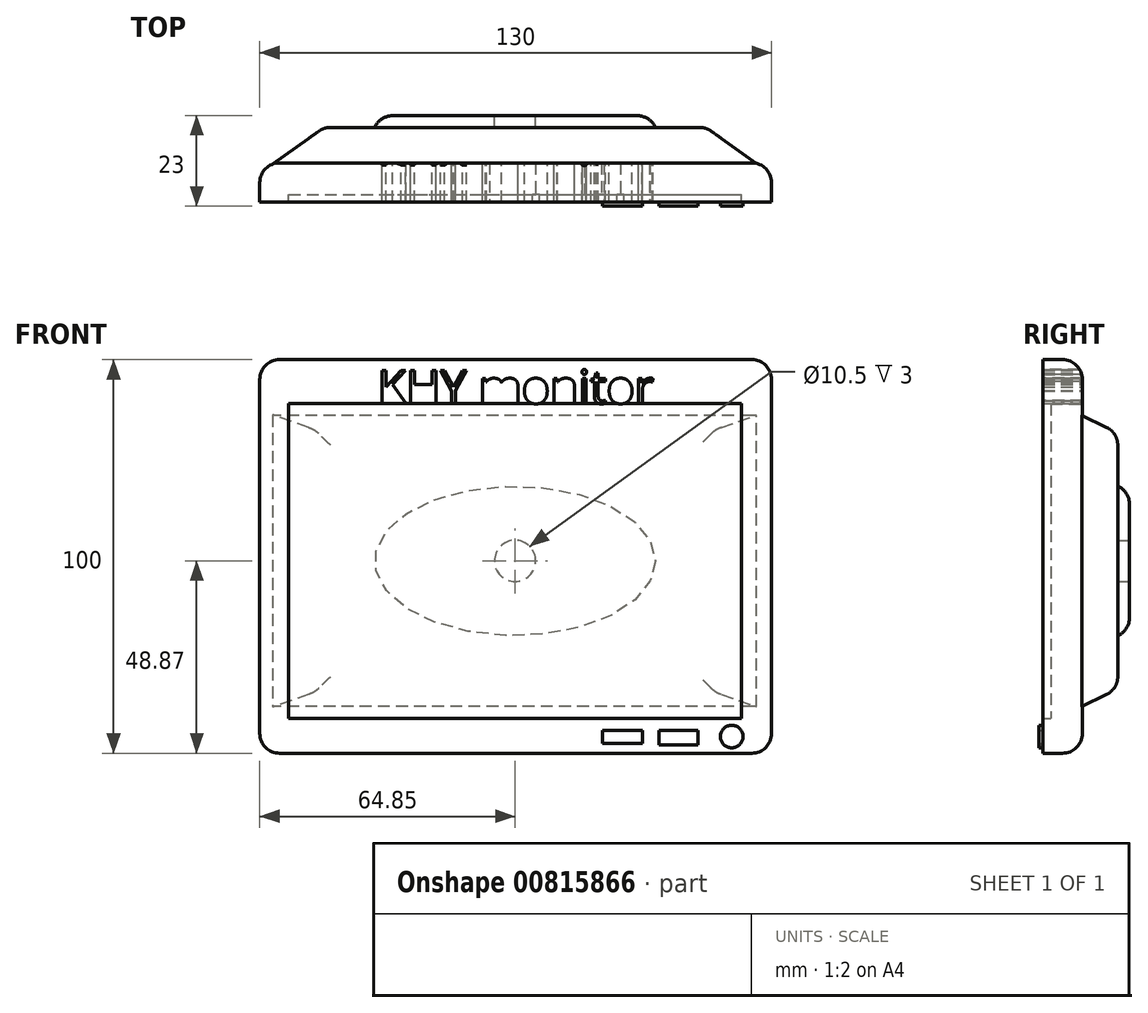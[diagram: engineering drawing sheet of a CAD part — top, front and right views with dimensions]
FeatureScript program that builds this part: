
annotation { "Feature Type Name" : "Feature", "Feature Type Description" : "" }
export const myFeature = defineFeature(function(context is Context, id is Id, definition is map)
    precondition{}
    {
        {
            var Q0;
            Q0=qCreatedBy(makeId("Front.planeOp"),FACE);
            var sketch = newSketch(context, id + "F0", { "sketchPlane" : qUnion([Q0])});
            skLineSegment(sketch, "E0.bottom", {"start": v(-59.85, 51.13) * mm, "end": v(60.15, 51.13) * mm});
            skLineSegment(sketch, "E0.top", {"start": v(-59.85, -48.87) * mm, "end": v(60.15, -48.87) * mm});
            skLineSegment(sketch, "E0.left", {"start": v(-64.85, 46.13) * mm, "end": v(-64.85, -43.87) * mm});
            skLineSegment(sketch, "E0.right", {"start": v(65.15, 46.13) * mm, "end": v(65.15, -43.87) * mm});
            skPoint(sketch, "E1.visualSharp", {"position": v(-64.85, 51.13) * mm});
            skArc(sketch, "E1.filletArc", {"start": v(-59.85, 51.13) * mm, "mid": v(-63.38, 49.67) * mm, "end": v(-64.85, 46.13) * mm});
            skPoint(sketch, "E2.visualSharp", {"position": v(65.15, 51.13) * mm});
            skArc(sketch, "E2.filletArc", {"start": v(65.15, 46.13) * mm, "mid": v(63.69, 49.67) * mm, "end": v(60.15, 51.13) * mm});
            skPoint(sketch, "E3.visualSharp", {"position": v(65.15, -48.87) * mm});
            skArc(sketch, "E3.filletArc", {"start": v(60.15, -48.87) * mm, "mid": v(63.69, -47.4) * mm, "end": v(65.15, -43.87) * mm});
            skPoint(sketch, "E4.visualSharp", {"position": v(-64.85, -48.87) * mm});
            skArc(sketch, "E4.filletArc", {"start": v(-64.85, -43.87) * mm, "mid": v(-63.38, -47.4) * mm, "end": v(-59.85, -48.87) * mm});
            skLineSegment(sketch, "E5.bottom", {"start": v(-57.5, 40) * mm, "end": v(57.5, 40) * mm});
            skLineSegment(sketch, "E5.top", {"start": v(-57.5, -40) * mm, "end": v(57.5, -40) * mm});
            skLineSegment(sketch, "E5.left", {"start": v(-57.5, 40) * mm, "end": v(-57.5, -40) * mm});
            skLineSegment(sketch, "E5.right", {"start": v(57.5, 40) * mm, "end": v(57.5, -40) * mm});
            skPoint(sketch, "E5.middle", {"position": v(0, 0) * mm});
            skText(sketch, "E6", { "text": "KHY monitor", "fontName": "OpenSans-Regular.ttf"});
            const initialGuessF0  = {"E6": [-0.0349, 0.04, 1, 0, 0.0085]};
            skSetInitialGuess(sketch, initialGuessF0);
            skSolve(sketch);
        }
        {
            var Q0;
            Q0=makeQuery(id+"F0.imprint","IMPRINT",FACE,{"disambiguationData":[TD([[makeQuery(id+"F0.imprint","IMPRINT",EDGE,{"derivedFrom":sQuery(id+"F0.wireOp",EDGE,"E0.bottom")}),-1.0]])]});
            extrude(context, id + "F1", {"entities" : qUnion([Q0]), "depth" : 10 * mm, "offsetDistance" : 25 * mm});
        }
        {
            var Q0;
            Q0=makeQuery(id+"F0.imprint","IMPRINT",FACE,{"disambiguationData":[TD([[makeQuery(id+"F0.imprint","IMPRINT",EDGE,{"derivedFrom":sQuery(id+"F0.wireOp",EDGE,"E5.top")}),1.0]])]});
            extrude(context, id + "F2", {"entities" : qUnion([Q0]), "operationType" : NewBodyOperationType.ADD, "depth" : 8 * mm, "offsetDistance" : 25 * mm});
        }
        {
            var Q0;
            Q0=qCreatedBy(makeId("Front.planeOp"),FACE);
            cPlane(context, id + "F3", {"entities" : qUnion([Q0]), "cplaneType" : CPlaneType.OFFSET, "offset" : 9 * mm, "oppositeDirection" : true, "width" : 150 * mm, "height" : 150 * mm});
        }
        {
            var Q0;
            Q0=qCreatedBy(id+"F3.planeOp",FACE);
            var sketch = newSketch(context, id + "F4", { "sketchPlane" : qUnion([Q0])});
            skLineSegment(sketch, "E7.bottom", {"start": v(48.52, 32.56) * mm, "end": v(-48.52, 32.56) * mm});
            skLineSegment(sketch, "E7.top", {"start": v(48.52, -32.56) * mm, "end": v(-48.52, -32.56) * mm});
            skLineSegment(sketch, "E7.left", {"start": v(48.52, 32.56) * mm, "end": v(48.52, -32.56) * mm});
            skLineSegment(sketch, "E7.right", {"start": v(-48.52, 32.56) * mm, "end": v(-48.52, -32.56) * mm});
            skPoint(sketch, "E7.middle", {"position": v(0, 0) * mm});
            skSolve(sketch);
        }
        {
            var Q0;
            Q0=qCreatedBy(makeId("Front.planeOp"),FACE);
            var sketch = newSketch(context, id + "F5", { "sketchPlane" : qUnion([Q0])});
            skLineSegment(sketch, "E8.bottom", {"start": v(61.13, 36.93) * mm, "end": v(-61.13, 36.93) * mm});
            skLineSegment(sketch, "E8.top", {"start": v(61.13, -36.93) * mm, "end": v(-61.13, -36.93) * mm});
            skLineSegment(sketch, "E8.left", {"start": v(61.13, 36.93) * mm, "end": v(61.13, -36.93) * mm});
            skLineSegment(sketch, "E8.right", {"start": v(-61.13, 36.93) * mm, "end": v(-61.13, -36.93) * mm});
            skPoint(sketch, "E8.middle", {"position": v(0, 0) * mm});
            skSolve(sketch);
        }
        {
            var Q1;
            Q1=makeQuery(id+"F4.imprint","IMPRINT",FACE,{"disambiguationData":[TD([[makeQuery(id+"F4.imprint","IMPRINT",EDGE,{"derivedFrom":sQuery(id+"F4.wireOp",EDGE,"E7.bottom")}),1.0]])]});
            var Q2;
            Q2=makeQuery(id+"F5.imprint","IMPRINT",FACE,{"disambiguationData":[TD([[makeQuery(id+"F5.imprint","IMPRINT",EDGE,{"derivedFrom":sQuery(id+"F5.wireOp",EDGE,"E8.bottom")}),1.0]])]});
            loft(context, id + "F6", {"operationType" : NewBodyOperationType.ADD, "sheetProfilesArray" : [{ "sheetProfileEntities" : qUnion([Q1]) }, { "sheetProfileEntities" : qUnion([Q2]) }]});
        }
        {
            var Q0;
            Q0=makeQuery(id+"F1.opExtrude","CAP_FACE",FACE,{"disambiguationData":[OSD([sQuery(id+"F0.wireOp",EDGE,"E0.bottom"),sQuery(id+"F0.wireOp",EDGE,"E0.top"),sQuery(id+"F0.wireOp",EDGE,"E0.left"),sQuery(id+"F0.wireOp",EDGE,"E0.right"),sQuery(id+"F0.wireOp",EDGE,"E1.filletArc"),sQuery(id+"F0.wireOp",EDGE,"E2.filletArc"),sQuery(id+"F0.wireOp",EDGE,"E3.filletArc"),sQuery(id+"F0.wireOp",EDGE,"E4.filletArc"),sQuery(id+"F0.wireOp",EDGE,"E5.bottom"),sQuery(id+"F0.wireOp",EDGE,"E5.top"),sQuery(id+"F0.wireOp",EDGE,"E5.left"),sQuery(id+"F0.wireOp",EDGE,"E5.right"),sQuery(id+"F0.wireOp",EDGE,"E6.sketch_text.stroke-5"),sQuery(id+"F0.wireOp",EDGE,"E6.sketch_text.stroke-6"),sQuery(id+"F0.wireOp",EDGE,"E6.sketch_text.stroke-7"),sQuery(id+"F0.wireOp",EDGE,"E6.sketch_text.stroke-8"),sQuery(id+"F0.wireOp",EDGE,"E6.sketch_text.stroke-9"),sQuery(id+"F0.wireOp",EDGE,"E6.sketch_text.stroke-10"),sQuery(id+"F0.wireOp",EDGE,"E6.sketch_text.stroke-11"),sQuery(id+"F0.wireOp",EDGE,"E6.sketch_text.stroke-17"),sQuery(id+"F0.wireOp",EDGE,"E6.sketch_text.stroke-18"),sQuery(id+"F0.wireOp",EDGE,"E6.sketch_text.stroke-19"),sQuery(id+"F0.wireOp",EDGE,"E6.sketch_text.stroke-20"),sQuery(id+"F0.wireOp",EDGE,"E6.sketch_text.stroke-21"),sQuery(id+"F0.wireOp",EDGE,"E6.sketch_text.stroke-22"),sQuery(id+"F0.wireOp",EDGE,"E6.sketch_text.stroke-23"),sQuery(id+"F0.wireOp",EDGE,"E6.sketch_text.stroke-24"),sQuery(id+"F0.wireOp",EDGE,"E6.sketch_text.stroke-25"),sQuery(id+"F0.wireOp",EDGE,"E6.sketch_text.stroke-26"),sQuery(id+"F0.wireOp",EDGE,"E6.sketch_text.stroke-27"),sQuery(id+"F0.wireOp",EDGE,"E6.sketch_text.stroke-29"),sQuery(id+"F0.wireOp",EDGE,"E6.sketch_text.stroke-30"),sQuery(id+"F0.wireOp",EDGE,"E6.sketch_text.stroke-31"),sQuery(id+"F0.wireOp",EDGE,"E6.sketch_text.stroke-32"),sQuery(id+"F0.wireOp",EDGE,"E6.sketch_text.stroke-47"),sQuery(id+"F0.wireOp",EDGE,"E6.sketch_text.stroke-48"),sQuery(id+"F0.wireOp",EDGE,"E6.sketch_text.stroke-49"),sQuery(id+"F0.wireOp",EDGE,"E6.sketch_text.stroke-50"),sQuery(id+"F0.wireOp",EDGE,"E6.sketch_text.stroke-51"),sQuery(id+"F0.wireOp",EDGE,"E6.sketch_text.stroke-52"),sQuery(id+"F0.wireOp",EDGE,"E6.sketch_text.stroke-53"),sQuery(id+"F0.wireOp",EDGE,"E6.sketch_text.stroke-54"),sQuery(id+"F0.wireOp",EDGE,"E6.sketch_text.stroke-55"),sQuery(id+"F0.wireOp",EDGE,"E6.sketch_text.stroke-56"),sQuery(id+"F0.wireOp",EDGE,"E6.sketch_text.stroke-57"),sQuery(id+"F0.wireOp",EDGE,"E6.sketch_text.stroke-58"),sQuery(id+"F0.wireOp",EDGE,"E6.sketch_text.stroke-59"),sQuery(id+"F0.wireOp",EDGE,"E6.sketch_text.stroke-61"),sQuery(id+"F0.wireOp",EDGE,"E6.sketch_text.stroke-62"),sQuery(id+"F0.wireOp",EDGE,"E6.sketch_text.stroke-63"),sQuery(id+"F0.wireOp",EDGE,"E6.sketch_text.stroke-64"),sQuery(id+"F0.wireOp",EDGE,"E6.sketch_text.stroke-65"),sQuery(id+"F0.wireOp",EDGE,"E6.sketch_text.stroke-66"),sQuery(id+"F0.wireOp",EDGE,"E6.sketch_text.stroke-67"),sQuery(id+"F0.wireOp",EDGE,"E6.sketch_text.stroke-68"),sQuery(id+"F0.wireOp",EDGE,"E6.sketch_text.stroke-69"),sQuery(id+"F0.wireOp",EDGE,"E6.sketch_text.stroke-85"),sQuery(id+"F0.wireOp",EDGE,"E6.sketch_text.stroke-86"),sQuery(id+"F0.wireOp",EDGE,"E6.sketch_text.stroke-87"),sQuery(id+"F0.wireOp",EDGE,"E6.sketch_text.stroke-88"),sQuery(id+"F0.wireOp",EDGE,"E6.sketch_text.stroke-89"),sQuery(id+"F0.wireOp",EDGE,"E6.sketch_text.stroke-90"),sQuery(id+"F0.wireOp",EDGE,"E6.sketch_text.stroke-91"),sQuery(id+"F0.wireOp",EDGE,"E6.sketch_text.stroke-92"),sQuery(id+"F0.wireOp",EDGE,"E6.sketch_text.stroke-93"),sQuery(id+"F0.wireOp",EDGE,"E6.sketch_text.stroke-96"),sQuery(id+"F0.wireOp",EDGE,"E6.sketch_text.stroke-97"),sQuery(id+"F0.wireOp",EDGE,"E6.sketch_text.stroke-98"),sQuery(id+"F0.wireOp",EDGE,"E6.sketch_text.stroke-99"),sQuery(id+"F0.wireOp",EDGE,"E6.sketch_text.stroke-100"),sQuery(id+"F0.wireOp",EDGE,"E6.sketch_text.stroke-101"),sQuery(id+"F0.wireOp",EDGE,"E6.sketch_text.stroke-102"),sQuery(id+"F0.wireOp",EDGE,"E6.sketch_text.stroke-103"),sQuery(id+"F0.wireOp",EDGE,"E6.sketch_text.stroke-104"),sQuery(id+"F0.wireOp",EDGE,"E6.sketch_text.stroke-105"),sQuery(id+"F0.wireOp",EDGE,"E6.sketch_text.stroke-106"),sQuery(id+"F0.wireOp",EDGE,"E6.sketch_text.stroke-107"),sQuery(id+"F0.wireOp",EDGE,"E6.sketch_text.stroke-108"),sQuery(id+"F0.wireOp",EDGE,"E6.sketch_text.stroke-109"),sQuery(id+"F0.wireOp",EDGE,"E6.sketch_text.stroke-110"),sQuery(id+"F0.wireOp",EDGE,"E6.sketch_text.stroke-112"),sQuery(id+"F0.wireOp",EDGE,"E6.sketch_text.stroke-113"),sQuery(id+"F0.wireOp",EDGE,"E6.sketch_text.stroke-114"),sQuery(id+"F0.wireOp",EDGE,"E6.sketch_text.stroke-115"),sQuery(id+"F0.wireOp",EDGE,"E6.sketch_text.stroke-116"),sQuery(id+"F0.wireOp",EDGE,"E6.sketch_text.stroke-117"),sQuery(id+"F0.wireOp",EDGE,"E6.sketch_text.stroke-118"),sQuery(id+"F0.wireOp",EDGE,"E6.sketch_text.stroke-119"),sQuery(id+"F0.wireOp",EDGE,"E6.sketch_text.stroke-120"),sQuery(id+"F0.wireOp",EDGE,"E6.sketch_text.stroke-121"),sQuery(id+"F0.wireOp",EDGE,"E6.sketch_text.stroke-122"),sQuery(id+"F0.wireOp",EDGE,"E6.sketch_text.stroke-123"),sQuery(id+"F0.wireOp",EDGE,"E6.sketch_text.stroke-124"),sQuery(id+"F0.wireOp",EDGE,"E6.sketch_text.stroke-125"),sQuery(id+"F0.wireOp",EDGE,"E6.sketch_text.stroke-126"),sQuery(id+"F0.wireOp",EDGE,"E6.sketch_text.stroke-127"),sQuery(id+"F0.wireOp",EDGE,"E6.sketch_text.stroke-128"),sQuery(id+"F0.wireOp",EDGE,"E6.sketch_text.stroke-129"),sQuery(id+"F0.wireOp",EDGE,"E6.sketch_text.stroke-130"),sQuery(id+"F0.wireOp",EDGE,"E6.sketch_text.stroke-131"),sQuery(id+"F0.wireOp",EDGE,"E6.sketch_text.stroke-132"),sQuery(id+"F0.wireOp",EDGE,"E6.sketch_text.stroke-133"),sQuery(id+"F0.wireOp",EDGE,"E6.sketch_text.stroke-134"),sQuery(id+"F0.wireOp",EDGE,"E6.sketch_text.stroke-143"),sQuery(id+"F0.wireOp",EDGE,"E6.sketch_text.stroke-144"),sQuery(id+"F0.wireOp",EDGE,"E6.sketch_text.stroke-145"),sQuery(id+"F0.wireOp",EDGE,"E6.sketch_text.stroke-146"),sQuery(id+"F0.wireOp",EDGE,"E6.sketch_text.stroke-147"),sQuery(id+"F0.wireOp",EDGE,"E6.sketch_text.stroke-148"),sQuery(id+"F0.wireOp",EDGE,"E6.sketch_text.stroke-150"),sQuery(id+"F0.wireOp",EDGE,"E6.sketch_text.stroke-151"),sQuery(id+"F0.wireOp",EDGE,"E6.sketch_text.stroke-152"),sQuery(id+"F0.wireOp",EDGE,"E6.sketch_text.stroke-153"),sQuery(id+"F0.wireOp",EDGE,"E6.sketch_text.stroke-154"),sQuery(id+"F0.wireOp",EDGE,"E6.sketch_text.stroke-155")])],"isStart":false});
            var sketch = newSketch(context, id + "F7", { "sketchPlane" : qUnion([Q0])});
            skCircle(sketch, "E9", {"center": v(52.28, -44.85) * mm, "radius": 3.24 * mm});
            skLineSegment(sketch, "E10.bottom", {"start": v(36.52, -43.04) * mm, "end": v(46.49, -43.04) * mm});
            skLineSegment(sketch, "E10.top", {"start": v(36.52, -46.8) * mm, "end": v(46.49, -46.8) * mm});
            skLineSegment(sketch, "E10.left", {"start": v(36.52, -43.04) * mm, "end": v(36.52, -46.8) * mm});
            skLineSegment(sketch, "E10.right", {"start": v(46.49, -43.04) * mm, "end": v(46.49, -46.8) * mm});
            skLineSegment(sketch, "E11.bottom", {"start": v(32.39, -43.04) * mm, "end": v(22.24, -43.04) * mm});
            skLineSegment(sketch, "E11.top", {"start": v(32.39, -46.42) * mm, "end": v(22.24, -46.42) * mm});
            skLineSegment(sketch, "E11.left", {"start": v(32.39, -43.04) * mm, "end": v(32.39, -46.42) * mm});
            skLineSegment(sketch, "E11.right", {"start": v(22.24, -43.04) * mm, "end": v(22.24, -46.42) * mm});
            skSolve(sketch);
        }
        {
            var Q0;
            Q0=makeQuery(id+"F7.imprint","IMPRINT",FACE,{"disambiguationData":[TD([[makeQuery(id+"F7.imprint","IMPRINT",EDGE,{"derivedFrom":sQuery(id+"F7.wireOp",EDGE,"E10.bottom")}),-1.0]])]});
            extrude(context, id + "F8", {"entities" : qUnion([Q0]), "operationType" : NewBodyOperationType.ADD, "depth" : 1 * mm, "offsetDistance" : 25 * mm});
        }
        {
            var Q0;
            Q0=makeQuery(id+"F7.imprint","IMPRINT",FACE,{"disambiguationData":[TD([[makeQuery(id+"F7.imprint","IMPRINT",EDGE,{"derivedFrom":sQuery(id+"F7.wireOp",EDGE,"E11.bottom")}),1.0]])]});
            extrude(context, id + "F9", {"entities" : qUnion([Q0]), "operationType" : NewBodyOperationType.ADD, "depth" : 1 * mm, "offsetDistance" : 25 * mm});
        }
        {
            var Q0;
            Q0=makeQuery(id+"F6.opLoft","CAP_FACE",FACE,{"disambiguationData":[OSD([makeQuery(id+"F4.imprint","IMPRINT",FACE,{"disambiguationData":[TD([[makeQuery(id+"F4.imprint","IMPRINT",EDGE,{"derivedFrom":sQuery(id+"F4.wireOp",EDGE,"E7.bottom")}),1.0]])]})])],"isStart":true});
            var sketch = newSketch(context, id + "F10", { "sketchPlane" : qUnion([Q0])});
            skEllipse(sketch, "E12", {"center": v(0, 0) * mm, "majorRadius": 35.66 * mm, "minorRadius": 18.99 * mm, "majorAxis": v(-1, 0)});
            skSolve(sketch);
        }
        {
            var Q0;
            Q0 = qSketchRegion(id + "F10", true);
            extrude(context, id + "F11", {"entities" : qUnion([Q0]), "operationType" : NewBodyOperationType.ADD, "depth" : 3 * mm, "offsetDistance" : 25 * mm});
        }
        {
            var Q0;
            Q0=makeQuery(id+"F11.opExtrude","CAP_FACE",FACE,{"disambiguationData":[OSD([sQuery(id+"F10.wireOp",EDGE,"E12")])],"isStart":false});
            fillet(context, id + "F12", {"entities" : qUnion([Q0]), "radius" : 5 * mm, "tangentPropagation" : true, "allowEdgeOverflow" : false});
        }
        {
            var Q0;
            Q0=makeQuery(id+"F11.opExtrude","CAP_FACE",FACE,{"disambiguationData":[OSD([sQuery(id+"F10.wireOp",EDGE,"E12")])],"isStart":false});
            var sketch = newSketch(context, id + "F13", { "sketchPlane" : qUnion([Q0])});
            skCircle(sketch, "E13", {"center": v(0, 0) * mm, "radius": 5.25 * mm});
            skSolve(sketch);
        }
        {
            var Q0;
            Q0 = qSketchRegion(id + "F13", true);
            extrude(context, id + "F14", {"entities" : qUnion([Q0]), "operationType" : NewBodyOperationType.REMOVE, "oppositeDirection" : true, "depth" : 3 * mm, "offsetDistance" : 25 * mm});
        }
        {
            var Q0;
            Q0=makeQuery(id+"F1.opExtrude","CAP_FACE",FACE,{"disambiguationData":[OSD([sQuery(id+"F0.wireOp",EDGE,"E0.bottom"),sQuery(id+"F0.wireOp",EDGE,"E0.top"),sQuery(id+"F0.wireOp",EDGE,"E0.left"),sQuery(id+"F0.wireOp",EDGE,"E0.right"),sQuery(id+"F0.wireOp",EDGE,"E1.filletArc"),sQuery(id+"F0.wireOp",EDGE,"E2.filletArc"),sQuery(id+"F0.wireOp",EDGE,"E3.filletArc"),sQuery(id+"F0.wireOp",EDGE,"E4.filletArc"),sQuery(id+"F0.wireOp",EDGE,"E5.bottom"),sQuery(id+"F0.wireOp",EDGE,"E5.top"),sQuery(id+"F0.wireOp",EDGE,"E5.left"),sQuery(id+"F0.wireOp",EDGE,"E5.right"),sQuery(id+"F0.wireOp",EDGE,"E6.sketch_text.stroke-5"),sQuery(id+"F0.wireOp",EDGE,"E6.sketch_text.stroke-6"),sQuery(id+"F0.wireOp",EDGE,"E6.sketch_text.stroke-7"),sQuery(id+"F0.wireOp",EDGE,"E6.sketch_text.stroke-8"),sQuery(id+"F0.wireOp",EDGE,"E6.sketch_text.stroke-9"),sQuery(id+"F0.wireOp",EDGE,"E6.sketch_text.stroke-10"),sQuery(id+"F0.wireOp",EDGE,"E6.sketch_text.stroke-11"),sQuery(id+"F0.wireOp",EDGE,"E6.sketch_text.stroke-17"),sQuery(id+"F0.wireOp",EDGE,"E6.sketch_text.stroke-18"),sQuery(id+"F0.wireOp",EDGE,"E6.sketch_text.stroke-19"),sQuery(id+"F0.wireOp",EDGE,"E6.sketch_text.stroke-20"),sQuery(id+"F0.wireOp",EDGE,"E6.sketch_text.stroke-21"),sQuery(id+"F0.wireOp",EDGE,"E6.sketch_text.stroke-22"),sQuery(id+"F0.wireOp",EDGE,"E6.sketch_text.stroke-23"),sQuery(id+"F0.wireOp",EDGE,"E6.sketch_text.stroke-24"),sQuery(id+"F0.wireOp",EDGE,"E6.sketch_text.stroke-25"),sQuery(id+"F0.wireOp",EDGE,"E6.sketch_text.stroke-26"),sQuery(id+"F0.wireOp",EDGE,"E6.sketch_text.stroke-27"),sQuery(id+"F0.wireOp",EDGE,"E6.sketch_text.stroke-29"),sQuery(id+"F0.wireOp",EDGE,"E6.sketch_text.stroke-30"),sQuery(id+"F0.wireOp",EDGE,"E6.sketch_text.stroke-31"),sQuery(id+"F0.wireOp",EDGE,"E6.sketch_text.stroke-32"),sQuery(id+"F0.wireOp",EDGE,"E6.sketch_text.stroke-47"),sQuery(id+"F0.wireOp",EDGE,"E6.sketch_text.stroke-48"),sQuery(id+"F0.wireOp",EDGE,"E6.sketch_text.stroke-49"),sQuery(id+"F0.wireOp",EDGE,"E6.sketch_text.stroke-50"),sQuery(id+"F0.wireOp",EDGE,"E6.sketch_text.stroke-51"),sQuery(id+"F0.wireOp",EDGE,"E6.sketch_text.stroke-52"),sQuery(id+"F0.wireOp",EDGE,"E6.sketch_text.stroke-53"),sQuery(id+"F0.wireOp",EDGE,"E6.sketch_text.stroke-54"),sQuery(id+"F0.wireOp",EDGE,"E6.sketch_text.stroke-55"),sQuery(id+"F0.wireOp",EDGE,"E6.sketch_text.stroke-56"),sQuery(id+"F0.wireOp",EDGE,"E6.sketch_text.stroke-57"),sQuery(id+"F0.wireOp",EDGE,"E6.sketch_text.stroke-58"),sQuery(id+"F0.wireOp",EDGE,"E6.sketch_text.stroke-59"),sQuery(id+"F0.wireOp",EDGE,"E6.sketch_text.stroke-61"),sQuery(id+"F0.wireOp",EDGE,"E6.sketch_text.stroke-62"),sQuery(id+"F0.wireOp",EDGE,"E6.sketch_text.stroke-63"),sQuery(id+"F0.wireOp",EDGE,"E6.sketch_text.stroke-64"),sQuery(id+"F0.wireOp",EDGE,"E6.sketch_text.stroke-65"),sQuery(id+"F0.wireOp",EDGE,"E6.sketch_text.stroke-66"),sQuery(id+"F0.wireOp",EDGE,"E6.sketch_text.stroke-67"),sQuery(id+"F0.wireOp",EDGE,"E6.sketch_text.stroke-68"),sQuery(id+"F0.wireOp",EDGE,"E6.sketch_text.stroke-69"),sQuery(id+"F0.wireOp",EDGE,"E6.sketch_text.stroke-85"),sQuery(id+"F0.wireOp",EDGE,"E6.sketch_text.stroke-86"),sQuery(id+"F0.wireOp",EDGE,"E6.sketch_text.stroke-87"),sQuery(id+"F0.wireOp",EDGE,"E6.sketch_text.stroke-88"),sQuery(id+"F0.wireOp",EDGE,"E6.sketch_text.stroke-89"),sQuery(id+"F0.wireOp",EDGE,"E6.sketch_text.stroke-90"),sQuery(id+"F0.wireOp",EDGE,"E6.sketch_text.stroke-91"),sQuery(id+"F0.wireOp",EDGE,"E6.sketch_text.stroke-92"),sQuery(id+"F0.wireOp",EDGE,"E6.sketch_text.stroke-93"),sQuery(id+"F0.wireOp",EDGE,"E6.sketch_text.stroke-96"),sQuery(id+"F0.wireOp",EDGE,"E6.sketch_text.stroke-97"),sQuery(id+"F0.wireOp",EDGE,"E6.sketch_text.stroke-98"),sQuery(id+"F0.wireOp",EDGE,"E6.sketch_text.stroke-99"),sQuery(id+"F0.wireOp",EDGE,"E6.sketch_text.stroke-100"),sQuery(id+"F0.wireOp",EDGE,"E6.sketch_text.stroke-101"),sQuery(id+"F0.wireOp",EDGE,"E6.sketch_text.stroke-102"),sQuery(id+"F0.wireOp",EDGE,"E6.sketch_text.stroke-103"),sQuery(id+"F0.wireOp",EDGE,"E6.sketch_text.stroke-104"),sQuery(id+"F0.wireOp",EDGE,"E6.sketch_text.stroke-105"),sQuery(id+"F0.wireOp",EDGE,"E6.sketch_text.stroke-106"),sQuery(id+"F0.wireOp",EDGE,"E6.sketch_text.stroke-107"),sQuery(id+"F0.wireOp",EDGE,"E6.sketch_text.stroke-108"),sQuery(id+"F0.wireOp",EDGE,"E6.sketch_text.stroke-109"),sQuery(id+"F0.wireOp",EDGE,"E6.sketch_text.stroke-110"),sQuery(id+"F0.wireOp",EDGE,"E6.sketch_text.stroke-112"),sQuery(id+"F0.wireOp",EDGE,"E6.sketch_text.stroke-113"),sQuery(id+"F0.wireOp",EDGE,"E6.sketch_text.stroke-114"),sQuery(id+"F0.wireOp",EDGE,"E6.sketch_text.stroke-115"),sQuery(id+"F0.wireOp",EDGE,"E6.sketch_text.stroke-116"),sQuery(id+"F0.wireOp",EDGE,"E6.sketch_text.stroke-117"),sQuery(id+"F0.wireOp",EDGE,"E6.sketch_text.stroke-118"),sQuery(id+"F0.wireOp",EDGE,"E6.sketch_text.stroke-119"),sQuery(id+"F0.wireOp",EDGE,"E6.sketch_text.stroke-120"),sQuery(id+"F0.wireOp",EDGE,"E6.sketch_text.stroke-121"),sQuery(id+"F0.wireOp",EDGE,"E6.sketch_text.stroke-122"),sQuery(id+"F0.wireOp",EDGE,"E6.sketch_text.stroke-123"),sQuery(id+"F0.wireOp",EDGE,"E6.sketch_text.stroke-124"),sQuery(id+"F0.wireOp",EDGE,"E6.sketch_text.stroke-125"),sQuery(id+"F0.wireOp",EDGE,"E6.sketch_text.stroke-126"),sQuery(id+"F0.wireOp",EDGE,"E6.sketch_text.stroke-127"),sQuery(id+"F0.wireOp",EDGE,"E6.sketch_text.stroke-128"),sQuery(id+"F0.wireOp",EDGE,"E6.sketch_text.stroke-129"),sQuery(id+"F0.wireOp",EDGE,"E6.sketch_text.stroke-130"),sQuery(id+"F0.wireOp",EDGE,"E6.sketch_text.stroke-131"),sQuery(id+"F0.wireOp",EDGE,"E6.sketch_text.stroke-132"),sQuery(id+"F0.wireOp",EDGE,"E6.sketch_text.stroke-133"),sQuery(id+"F0.wireOp",EDGE,"E6.sketch_text.stroke-134"),sQuery(id+"F0.wireOp",EDGE,"E6.sketch_text.stroke-143"),sQuery(id+"F0.wireOp",EDGE,"E6.sketch_text.stroke-144"),sQuery(id+"F0.wireOp",EDGE,"E6.sketch_text.stroke-145"),sQuery(id+"F0.wireOp",EDGE,"E6.sketch_text.stroke-146"),sQuery(id+"F0.wireOp",EDGE,"E6.sketch_text.stroke-147"),sQuery(id+"F0.wireOp",EDGE,"E6.sketch_text.stroke-148"),sQuery(id+"F0.wireOp",EDGE,"E6.sketch_text.stroke-150"),sQuery(id+"F0.wireOp",EDGE,"E6.sketch_text.stroke-151"),sQuery(id+"F0.wireOp",EDGE,"E6.sketch_text.stroke-152"),sQuery(id+"F0.wireOp",EDGE,"E6.sketch_text.stroke-153"),sQuery(id+"F0.wireOp",EDGE,"E6.sketch_text.stroke-154"),sQuery(id+"F0.wireOp",EDGE,"E6.sketch_text.stroke-155")])],"isStart":false});
            var sketch = newSketch(context, id + "F15", { "sketchPlane" : qUnion([Q0])});
            skCircle(sketch, "E14", {"center": v(55.04, -44.62) * mm, "radius": 2.87 * mm});
            skSolve(sketch);
        }
        {
            var Q0;
            Q0 = qSketchRegion(id + "F15", true);
            extrude(context, id + "F16", {"entities" : qUnion([Q0]), "operationType" : NewBodyOperationType.ADD, "depth" : 1 * mm, "offsetDistance" : 25 * mm});
        }
        {
            var Q0;
            Q0=makeQuery(id+"F1.opExtrude","CAP_EDGE",EDGE,{"disambiguationData":[OSD([sQuery(id+"F0.wireOp",EDGE,"E0.right")])],"isStart":true});
            var Q1;
            Q1=makeQuery(id+"F1.opExtrude","CAP_EDGE",EDGE,{"disambiguationData":[OSD([sQuery(id+"F0.wireOp",EDGE,"E0.left")])],"isStart":true});
            var Q2;
            Q2=makeQuery(id+"F6.opLoft","MID_CAP_EDGE",EDGE,{"disambiguationData":[OSD([sQuery(id+"F4.wireOp",EDGE,"E7.bottom"),sQuery(id+"F4.wireOp",EDGE,"E7.top"),sQuery(id+"F4.wireOp",EDGE,"E7.right")])],"capPos":0.0});
            var Q3;
            Q3=makeQuery(id+"F6.opLoft","MID_CAP_EDGE",EDGE,{"disambiguationData":[OSD([sQuery(id+"F4.wireOp",EDGE,"E7.bottom"),sQuery(id+"F4.wireOp",EDGE,"E7.top"),sQuery(id+"F4.wireOp",EDGE,"E7.left")])],"capPos":0.0});
            var Q4;
            Q4=makeQuery(id+"F6.opLoft","MID_CAP_EDGE",EDGE,{"disambiguationData":[OSD([sQuery(id+"F4.wireOp",EDGE,"E7.top"),sQuery(id+"F4.wireOp",EDGE,"E7.left"),sQuery(id+"F4.wireOp",EDGE,"E7.right")])],"capPos":0.0});
            var Q5;
            Q5=makeQuery(id+"F6.opLoft","MID_CAP_EDGE",EDGE,{"disambiguationData":[OSD([sQuery(id+"F4.wireOp",EDGE,"E7.bottom"),sQuery(id+"F4.wireOp",EDGE,"E7.left"),sQuery(id+"F4.wireOp",EDGE,"E7.right")])],"capPos":0.0});
            fillet(context, id + "F17", {"entities" : qUnion([Q0, Q1, Q2, Q3, Q4, Q5]), "radius" : 5 * mm, "tangentPropagation" : true, "allowEdgeOverflow" : false});
        }
    });
